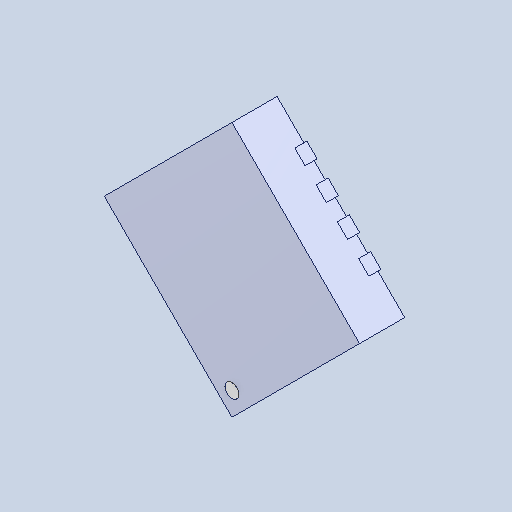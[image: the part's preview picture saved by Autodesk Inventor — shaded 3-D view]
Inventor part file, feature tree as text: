
AUTODESK INVENTOR PART (.ipt)
format: ipt  version: 2025 (Build 290162000, 162)  size: 233,472 bytes
history: native  units: mm
features: other x17, chamfer x2
ambient origin geometry x8: Origin, YZ Plane, XZ Plane, XY Plane, X Axis, Y Axis, Z Axis, Center Point
bodies: Solid1 (feature_tree), Solid2 (feature_tree), Solid3 (feature_tree), Solid4 (feature_tree), Solid5 (feature_tree), Solid6 (feature_tree), Solid7 (feature_tree), Solid8 (feature_tree), Solid9 (feature_tree), Solid10 (feature_tree), Solid11 (feature_tree), Solid12 (feature_tree), Solid13 (feature_tree), Solid14 (feature_tree), Solid15 (feature_tree), Solid16 (feature_tree), Solid17 (feature_tree), Solid18 (feature_tree), Solid19 (feature_tree)
feature tree (19):
  other  "LPattern4[4]"
  other  "LPattern3[4]"
  chamfer  "Chamfer2"  [1 undecoded]
  other  "LPattern4[1]"
  chamfer  "Chamfer1"  [1 undecoded]
  other  "Boss-Extrude2[2]"
  other  "LPattern3[3]"
  other  "LPattern4[5]"
  other  "Boss-Extrude3[2]"
  other  "LPattern3[5]"
  other  "LPattern4[3]"
  other  "LPattern3[1]"
  other  "Boss-Extrude3[1]"
  other  "LPattern4[2]"
  other  "LPattern3[6]"
  other  "LPattern3[2]"
  other  "LPattern4[6]"
  other  "Boss-Extrude2[1]"
  other  "PIN1"
note: 2 required parameter values undecoded (feature->parameter linkage not recoverable at this tier; creation-order binding heuristic only, values carry confidence <= 0.55)
